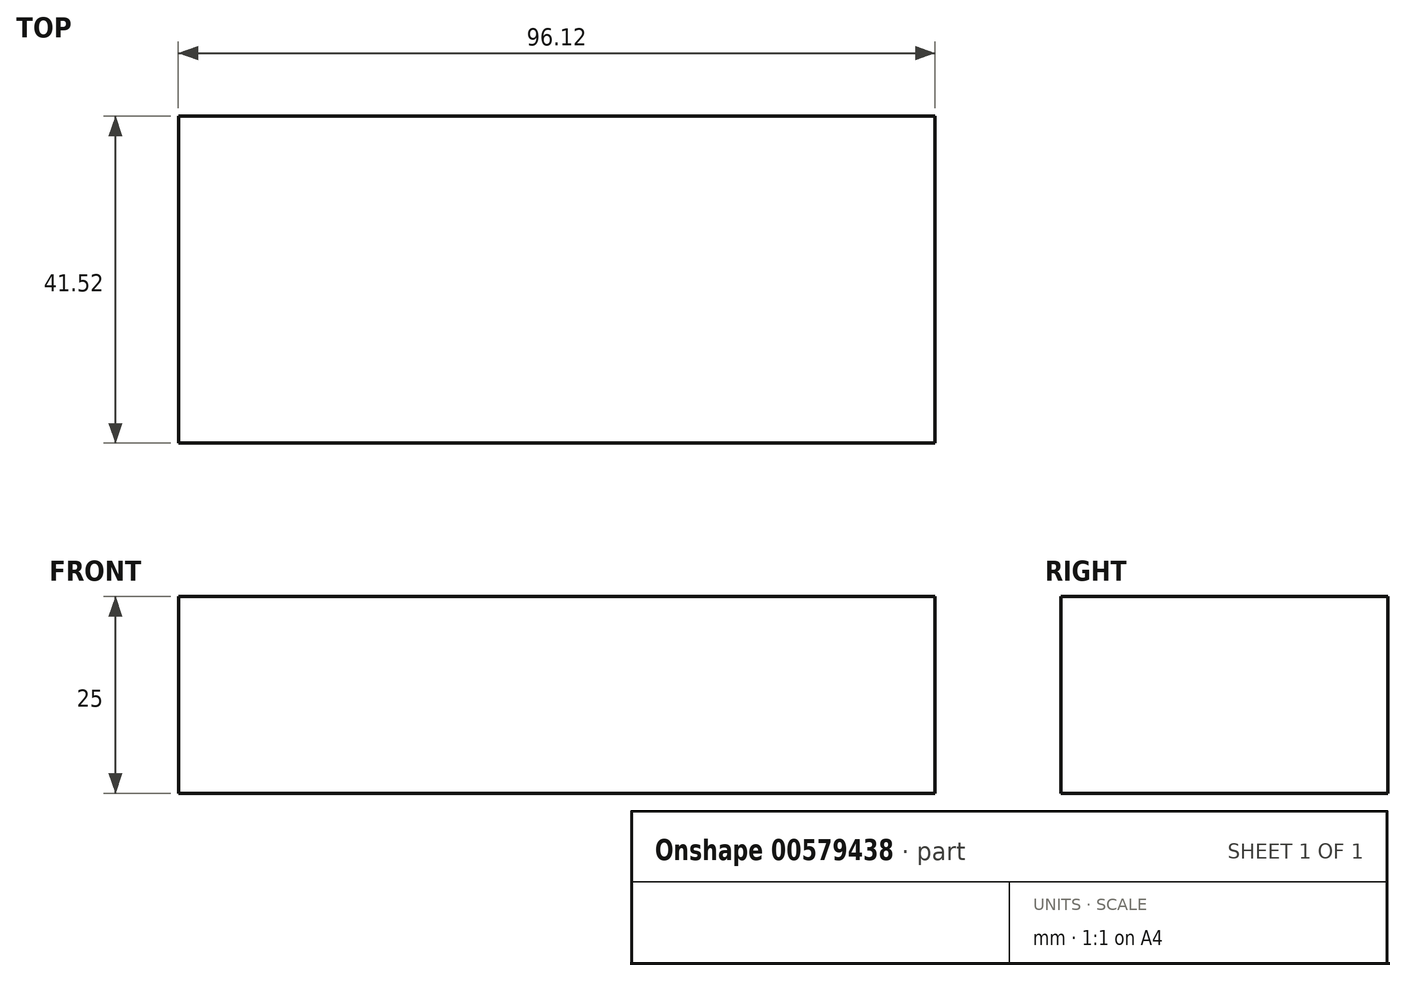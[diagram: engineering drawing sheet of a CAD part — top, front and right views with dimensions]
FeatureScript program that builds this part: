
annotation { "Feature Type Name" : "Feature", "Feature Type Description" : "" }
export const myFeature = defineFeature(function(context is Context, id is Id, definition is map)
    precondition{}
    {
        {
            var Q0;
            Q0=qCreatedBy(makeId("Top.planeOp"),FACE);
            var sketch = newSketch(context, id + "F0", { "sketchPlane" : qUnion([Q0])});
            skLineSegment(sketch, "E0.bottom", {"start": v(-48.06, 20.76) * mm, "end": v(48.06, 20.76) * mm});
            skLineSegment(sketch, "E0.top", {"start": v(-48.06, -20.76) * mm, "end": v(48.06, -20.76) * mm});
            skLineSegment(sketch, "E0.left", {"start": v(-48.06, 20.76) * mm, "end": v(-48.06, -20.76) * mm});
            skLineSegment(sketch, "E0.right", {"start": v(48.06, 20.76) * mm, "end": v(48.06, -20.76) * mm});
            skPoint(sketch, "E0.middle", {"position": v(0, 0) * mm});
            skSolve(sketch);
        }
        {
            var Q0;
            Q0 = qSketchRegion(id + "F0", true);
            extrude(context, id + "F1", {"entities" : qUnion([Q0]), "depth" : 25 * mm, "offsetDistance" : 25 * mm});
        }
        {
            var Q0;
            Q0=makeQuery(id+"F1.opExtrude","CAP_FACE",FACE,{"disambiguationData":[OSD([sQuery(id+"F0.wireOp",EDGE,"E0.bottom"),sQuery(id+"F0.wireOp",EDGE,"E0.top"),sQuery(id+"F0.wireOp",EDGE,"E0.left"),sQuery(id+"F0.wireOp",EDGE,"E0.right")])],"isStart":false});
            var sketch = newSketch(context, id + "F2", { "sketchPlane" : qUnion([Q0])});
            skLineSegment(sketch, "E1", {"start": v(-33.12, 8.08) * mm, "end": v(-33.12, -12.12) * mm});
            skLineSegment(sketch, "E2", {"start": v(-42.55, 8.08) * mm, "end": v(-20.2, 8.08) * mm});
            skLineSegment(sketch, "E3", {"start": v(-11.97, 8.08) * mm, "end": v(-11.97, -12.12) * mm});
            skPoint(sketch, "E3.startSnap0", {"position": v(-31.37, 8.08) * mm});
            skLineSegment(sketch, "E4", {"start": v(-11.97, -12.12) * mm, "end": v(0, -12.12) * mm});
            skLineSegment(sketch, "E5", {"start": v(-11.97, -2.02) * mm, "end": v(0, -2.02) * mm});
            skLineSegment(sketch, "E6", {"start": v(-11.97, 8.08) * mm, "end": v(0, 8.08) * mm});
            skLineSegment(sketch, "E7", {"start": v(7.24, 8.08) * mm, "end": v(15.41, -12.12) * mm});
            skLineSegment(sketch, "E8", {"start": v(15.41, 8.08) * mm, "end": v(7.24, -12.12) * mm});
            skLineSegment(sketch, "E9", {"start": v(23.9, 8.08) * mm, "end": v(34.62, 8.08) * mm});
            skLineSegment(sketch, "E10", {"start": v(29.26, 8.08) * mm, "end": v(29.26, -12.12) * mm});
            skSolve(sketch);
        }
        {
            var Q0;
            Q0 = qSketchRegion(id + "F2", true);
            var Q1;
            Q1=sQuery(id+"F2.wireOp",EDGE,"E1");
            var Q2;
            Q2=sQuery(id+"F2.wireOp",EDGE,"E6");
            var Q3;
            Q3=sQuery(id+"F2.wireOp",EDGE,"E5");
            var Q4;
            Q4=sQuery(id+"F2.wireOp",EDGE,"E4");
            var Q5;
            Q5=sQuery(id+"F2.wireOp",EDGE,"E8");
            var Q6;
            Q6=sQuery(id+"F2.wireOp",EDGE,"E10");
            extrude(context, id + "F3", {"entities" : qUnion([Q0]), "bodyType" : ExtendedToolBodyType.SURFACE, "surfaceEntities" : qUnion([Q1, Q2, Q3, Q4, Q5, Q6]), "depth" : 25 * mm, "offsetDistance" : 25 * mm, "symmetric" : true});
        }
        {
            var Q0;
            Q0=sQuery(id+"F2.wireOp",EDGE,"E2");
            var Q1;
            Q1=sQuery(id+"F2.wireOp",EDGE,"E3");
            var Q2;
            Q2=sQuery(id+"F2.wireOp",EDGE,"E7");
            var Q3;
            Q3=sQuery(id+"F2.wireOp",EDGE,"E9");
            extrude(context, id + "F4", {"bodyType" : ExtendedToolBodyType.SURFACE, "surfaceEntities" : qUnion([Q0, Q1, Q2, Q3]), "depth" : 25 * mm, "offsetDistance" : 25 * mm, "symmetric" : true});
        }
        {
            var Q0;
            Q0=makeQuery(id+"F2.imprint","IMPRINT",FACE,{"disambiguationData":[TD([[makeQuery(id+"F2.imprint","IMPRINT",EDGE,{"derivedFrom":makeQuery(id+"F1.opExtrude","CAP_EDGE",EDGE,{"disambiguationData":[OSD([sQuery(id+"F0.wireOp",EDGE,"E0.bottom")])],"isStart":false})}),-1.0]])]});
            cPlane(context, id + "F5", {"entities" : qUnion([Q0]), "cplaneType" : CPlaneType.OFFSET, "offset" : 25 * mm, "width" : 150 * mm, "height" : 150 * mm});
        }
    });
